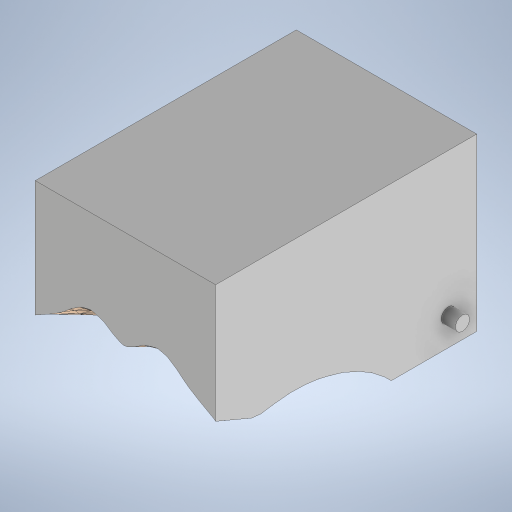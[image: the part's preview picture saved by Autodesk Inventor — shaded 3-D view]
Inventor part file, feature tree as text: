
AUTODESK INVENTOR PART (.ipt)
format: ipt  version: 2024 (Build 280153000, 153)  size: 10,929,152 bytes
history: native  units: mm
features: other x6, sketch x5, extrude x4, plane x2
ambient origin geometry x8: Origin, YZ Plane, XZ Plane, XY Plane, X Axis, Y Axis, Z Axis, Center Point
bodies: Body1 (feature_tree)
feature tree (17):
  other  "M.ipt"
  plane  "Plano de trabajo1"
  extrude  "Extrusión1"  [1 undecoded]
  other  "Combinar1"
  sketch  "Boceto3"  dims[d2=550.0mm d3=520.0mm]
  sketch  "Boceto4"  dims[d4=550.0mm d5=0.0mm d6=129.8482mm]
  plane  "Plano de trabajo2"
  sketch  "Boceto5"  dims[d17=180.0mm d18=180.0mm]
  extrude  "Extrusión2"  Depth=520.0mm
  extrude  "Extrusión3"  Depth=129.8482mm
  extrude  "Extrusión4"  Depth=180.0mm
  other  "Sólido1::M.ipt"
  other  "OperaciónIdentificador1"
  sketch  "Boceto1"  dims[d0=25.0mm d1=-365.0mm]
  other  "Sólido2"
  sketch  "Boceto6"  dims[d22=326.0mm d23=180.0mm d24=180.0mm d25=180.0mm d26=10.0mm d27=0.0mm d28=1000.0mm d29=0.0mm d30=30.0mm d31=30.0mm d32=15.0mm d33=15.0mm d34=205.0mm d35=0.0mm d36=0.0mm d14=0.5mm d15=0.872665mm d16=0.5mm d19=0.5mm d20=0.872665mm d21=0.5mm]
  other  "Sólido1"
note: 1 required parameter value undecoded (feature->parameter linkage not recoverable at this tier; creation-order binding heuristic only, values carry confidence <= 0.55)
